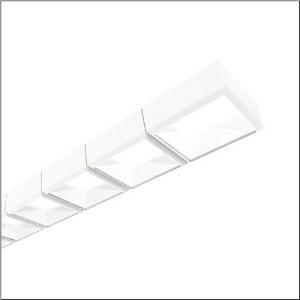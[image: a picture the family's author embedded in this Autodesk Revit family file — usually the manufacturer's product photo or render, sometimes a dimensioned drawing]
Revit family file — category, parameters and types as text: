
# Revit family: scriptus_r__11_5mz212d03wa_20e5
name_source: partatom
category: Lighting Fixtures
units: mm (PartAtom-declared; Revit-internal decimal feet)

## family parameters
Cut with Voids When Loaded = No
Host = Face
Light Source = No
Part Type = Normal
Room Calculation Point = No
Round Connector Dimension = Use Diameter
Shared = No

## types (1)
- Scriptus® 11 (1 x LED 3000K / CRI = 80 (unbekannt), 2200 lm, 3000K)
    Apparent Load = 35 VA
    CIE Flux Codes = 82 95 99 100 100
    Color Rendering = 80
    Color Temperature = 3000K
    Default Elevation = 1800 mm
    Description = Scriptus® 11, office luminaire, primary optical cover: lenses, CAT 2 (L<= 3000cd/m²), light emission: direct distribution, primary light characteristic: symmetric, installation type: surface-mounted, LED, rated luminous flux: 4.390lm, luminous efficacy: 127lm/W, light colour: 830, colour temperature: 3000K, control gear: DALI, with terminal, 5-pole, mains connection: 230V, AC, 50Hz, rated input power: 35W, housing, luminaire housing, of aluminium, traffic white (RAL 9016), length: 1.658mm, width: 114mm, height: 57mm, protection rating (complete): IP20, insulation class (complete): insulation class I (protective earthing), certification: CE, ENEC, VDE, protection symbol: F, permissible operating ambient temperature: 0..+35°C, standard: EN 50419, packaging unit: 1 piece
    Height = 57 mm
    Lamp = 1 x LED 3000K / CRI >= 80 (unbekannt)
    Lamp Light Flux = 2200 lm
    Lamp count = 1
    Length = 1658 mm
    Luminous efficacy = 127 lm/W
    Manufacturer = Siteco
    ModVariant = No
    Model = 5MZ212D03WA
    Mounting Place = Ceiling
    Mounting Type = Surface mounted
    Number of Poles = 1
    OnlyDefault = Yes
    Power Factor = 1
    Product Name = Scriptus® 11
    Product group = office luminaire | ceiling mounted
    ProductGroupID = 303
    Protection Class = Protection class I
    Protection Degree = IP 20
    RLX_Detail_Level = 1
    RLX_Emergency_Light_Flux = 0 lm
    RLX_Emergency_Type = 0
    RLX_Emergency_Type_DB = No
    RlxData = <blob elided: 29465 chars, md5=88643589>
    Socket = socket
    Standby Power = 0 W
    System Light Flux = 4400 lm
    System Power = 35 W
    Type Comments = Product without accessories
    Type Image = l_1004833.jpg
    URL = http://relux.com
    VarID = ---
    Voltage = 0 V
    Weight = 0.00 kg
    Width = 114 mm

## geometry (parser evidence)
native form markers: Blend x4, Sweep x13
no freeform markers — native parametric forms only
